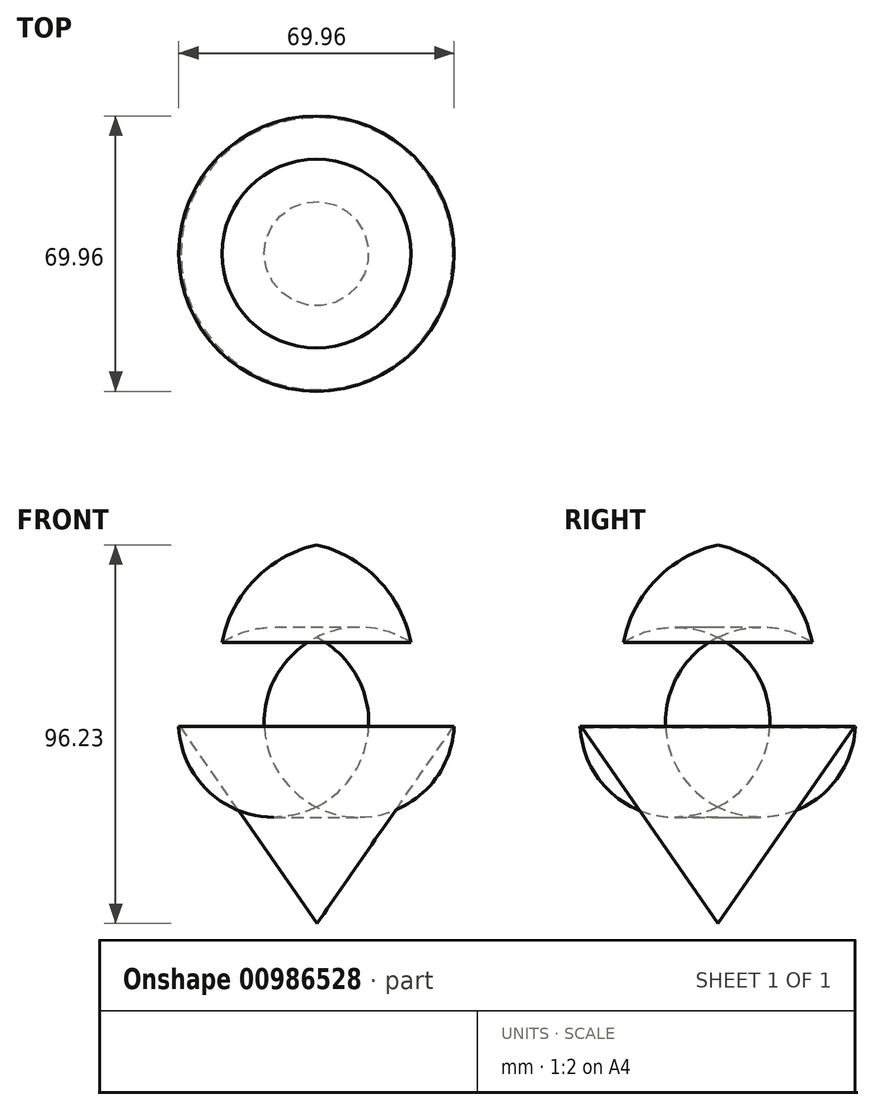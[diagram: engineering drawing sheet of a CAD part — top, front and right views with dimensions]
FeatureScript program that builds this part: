
annotation { "Feature Type Name" : "Feature", "Feature Type Description" : "" }
export const myFeature = defineFeature(function(context is Context, id is Id, definition is map)
    precondition{}
    {
        {
            var Q0;
            Q0=qCreatedBy(makeId("Front.planeOp"),FACE);
            var sketch = newSketch(context, id + "F0", { "sketchPlane" : qUnion([Q0])});
            skLineSegment(sketch, "E0", {"start": v(34.66, 25.65) * mm, "end": v(0.13, 25.65) * mm});
            skLineSegment(sketch, "E1", {"start": v(0.13, 25.65) * mm, "end": v(0.13, -24.14) * mm});
            skLineSegment(sketch, "E2", {"start": v(34.66, 25.65) * mm, "end": v(0.13, -24.14) * mm});
            skSolve(sketch);
        }
        {
            var Q0;
            Q0 = qSketchRegion(id + "F0", true);
            var Q1;
            Q1=sQuery(id+"F0.wireOp",EDGE,"E1");
            revolve(context, id + "F1", {"surfaceOperationType" : NewSurfaceOperationType.NEW, "entities" : qUnion([Q0]), "axis" : qUnion([Q1]), "revolveType" : RevolveType.FULL});
        }
        {
            var Q0;
            Q0=qCreatedBy(makeId("Right.planeOp"),FACE);
            var sketch = newSketch(context, id + "F2", { "sketchPlane" : qUnion([Q0])});
            skArc(sketch, "E3", {"start": v(34.98, 25.92) * mm, "mid": v(23.98, 47.27) * mm, "end": v(0, 48.56) * mm});
            skArc(sketch, "E4", {"start": v(23.98, 47.27) * mm, "mid": v(15.66, 63.23) * mm, "end": v(0, 72.1) * mm});
            skLineSegment(sketch, "E5", {"start": v(0, 72.1) * mm, "end": v(0, 25.92) * mm});
            skLineSegment(sketch, "E6", {"start": v(0, 25.92) * mm, "end": v(34.98, 25.92) * mm});
            skSolve(sketch);
        }
        {
            var Q0;
            Q0=qCreatedBy(makeId("Front.planeOp"),FACE);
            var sketch = newSketch(context, id + "F3", { "sketchPlane" : qUnion([Q0])});
            skLineSegment(sketch, "E7", {"start": v(0, -32.2) * mm, "end": v(0, -52.87) * mm});
            skSolve(sketch);
        }
        {
            var Q0;
            {var subQ3=sQuery(id+"F2.wireOp",EDGE,"E4");Q0=makeQuery(id+"F2.imprint","IMPRINT",FACE,{"disambiguationData":[TD([[makeQuery(id+"F2.imprint","IMPRINT",EDGE,{"derivedFrom":subQ3}),1.0]])]});}
            var Q1;
            {var subQ0=sQuery(id+"F2.wireOp",EDGE,"E6");Q1=makeQuery(id+"F2.imprint","IMPRINT",FACE,{"disambiguationData":[TD([[makeQuery(id+"F2.imprint","IMPRINT",EDGE,{"derivedFrom":subQ0}),1.0]])]});}
            var Q2;
            Q2=sQuery(id+"F3.wireOp",EDGE,"E7");
            revolve(context, id + "F4", {"surfaceOperationType" : NewSurfaceOperationType.NEW, "entities" : qUnion([Q0, Q1]), "axis" : qUnion([Q2]), "revolveType" : RevolveType.FULL});
        }
    });
